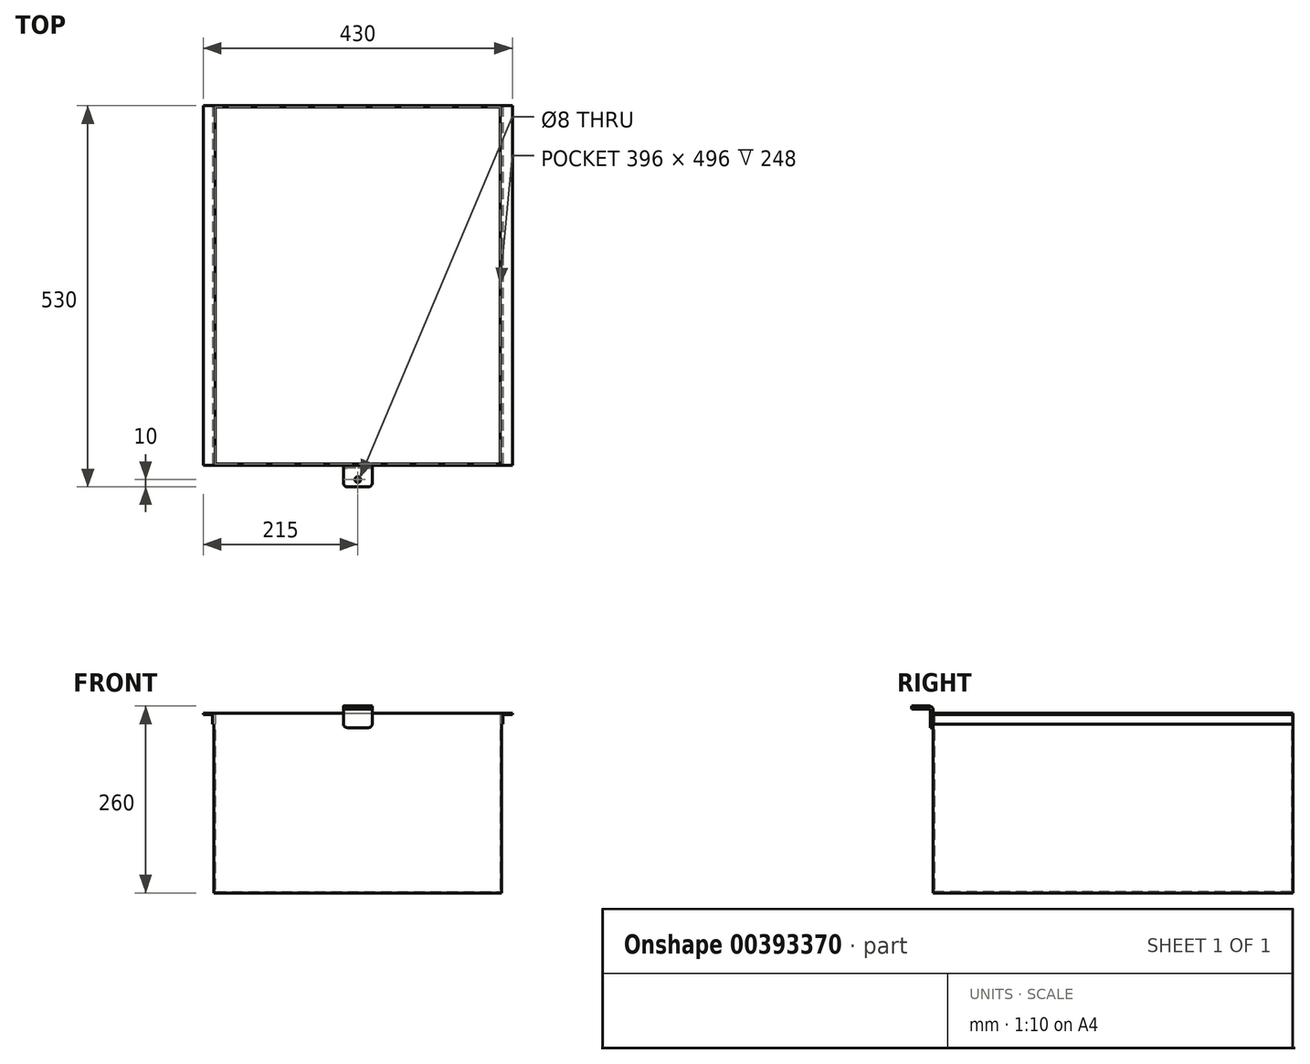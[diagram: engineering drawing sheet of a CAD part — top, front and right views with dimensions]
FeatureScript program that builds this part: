
annotation { "Feature Type Name" : "Feature", "Feature Type Description" : "" }
export const myFeature = defineFeature(function(context is Context, id is Id, definition is map)
    precondition{}
    {
        {
            var Q0;
            Q0=qCreatedBy(makeId("Top.planeOp"),FACE);
            var sketch = newSketch(context, id + "F0", { "sketchPlane" : qUnion([Q0])});
            skLineSegment(sketch, "E0.bottom", {"start": v(-200, 250) * mm, "end": v(200, 250) * mm});
            skLineSegment(sketch, "E0.top", {"start": v(-200, -250) * mm, "end": v(200, -250) * mm});
            skLineSegment(sketch, "E0.left", {"start": v(-200, 250) * mm, "end": v(-200, -250) * mm});
            skLineSegment(sketch, "E0.right", {"start": v(200, 250) * mm, "end": v(200, -250) * mm});
            skSolve(sketch);
        }
        {
            var Q0;
            Q0 = qSketchRegion(id + "F0", true);
            extrude(context, id + "F1", {"entities" : qUnion([Q0]), "depth" : 2 * mm, "offsetDistance" : 25 * mm});
        }
        {
            var Q0;
            Q0=makeQuery(id+"F1.opExtrude","CAP_FACE",FACE,{"disambiguationData":[OSD([sQuery(id+"F0.wireOp",EDGE,"E0.bottom"),sQuery(id+"F0.wireOp",EDGE,"E0.top"),sQuery(id+"F0.wireOp",EDGE,"E0.left"),sQuery(id+"F0.wireOp",EDGE,"E0.right")])],"isStart":false});
            var sketch = newSketch(context, id + "F2", { "sketchPlane" : qUnion([Q0])});
            skLineSegment(sketch, "E1.bottom", {"start": v(-200, 250) * mm, "end": v(200, 250) * mm});
            skLineSegment(sketch, "E1.top", {"start": v(-200, -250) * mm, "end": v(200, -250) * mm});
            skLineSegment(sketch, "E1.left", {"start": v(-200, 250) * mm, "end": v(-200, -250) * mm});
            skLineSegment(sketch, "E1.right", {"start": v(200, 250) * mm, "end": v(200, -250) * mm});
            skLineSegment(sketch, "E2.bottom", {"start": v(-198, 248) * mm, "end": v(198, 248) * mm});
            skLineSegment(sketch, "E2.top", {"start": v(-198, -248) * mm, "end": v(198, -248) * mm});
            skLineSegment(sketch, "E2.left", {"start": v(-198, 248) * mm, "end": v(-198, -248) * mm});
            skLineSegment(sketch, "E2.right", {"start": v(198, 248) * mm, "end": v(198, -248) * mm});
            skSolve(sketch);
        }
        {
            var Q0;
            Q0 = qSketchRegion(id + "F2", true);
            extrude(context, id + "F3", {"entities" : qUnion([Q0]), "operationType" : NewBodyOperationType.ADD, "depth" : 248 * mm, "offsetDistance" : 25 * mm});
        }
        {
            var Q0;
            Q0=makeQuery(id+"F3.boolean.opBoolean","MERGE",FACE,{"derivedFrom":[makeQuery(id+"F1.opExtrude","SWEPT_FACE",FACE,{"disambiguationData":[OSD([sQuery(id+"F0.wireOp",EDGE,"E0.top")])]}),makeQuery(id+"F3.opExtrude","SWEPT_FACE",FACE,{"disambiguationData":[OSD([sQuery(id+"F2.wireOp",EDGE,"E1.top")])]})]});
            var sketch = newSketch(context, id + "F4", { "sketchPlane" : qUnion([Q0])});
            skLineSegment(sketch, "E3", {"start": v(200, 250) * mm, "end": v(215, 250) * mm});
            skLineSegment(sketch, "E4", {"start": v(215, 250) * mm, "end": v(215, 248) * mm});
            skLineSegment(sketch, "E5", {"start": v(215, 248) * mm, "end": v(202, 248) * mm});
            skLineSegment(sketch, "E6", {"start": v(202, 248) * mm, "end": v(202, 235) * mm});
            skLineSegment(sketch, "E7", {"start": v(202, 235) * mm, "end": v(200, 235) * mm});
            skLineSegment(sketch, "E8", {"start": v(200, 235) * mm, "end": v(200, 250) * mm});
            skLineSegment(sketch, "E9.MirrorCS", {"start": v(-200, 250) * mm, "end": v(-215, 250) * mm});
            skLineSegment(sketch, "E10.MirrorCS", {"start": v(-215, 250) * mm, "end": v(-215, 248) * mm});
            skLineSegment(sketch, "E11.MirrorCS", {"start": v(-215, 248) * mm, "end": v(-202, 248) * mm});
            skLineSegment(sketch, "E12.MirrorCS", {"start": v(-202, 248) * mm, "end": v(-202, 235) * mm});
            skLineSegment(sketch, "E13.MirrorCS", {"start": v(-202, 235) * mm, "end": v(-200, 235) * mm});
            skLineSegment(sketch, "E14.MirrorCS", {"start": v(-200, 235) * mm, "end": v(-200, 250) * mm});
            skSolve(sketch);
        }
        {
            var Q0;
            Q0 = qSketchRegion(id + "F4", true);
            extrude(context, id + "F5", {"entities" : qUnion([Q0]), "operationType" : NewBodyOperationType.ADD, "oppositeDirection" : true, "depth" : 500 * mm, "offsetDistance" : 25 * mm});
        }
        {
            var Q0;
            Q0=qCreatedBy(makeId("Right.planeOp"),FACE);
            var sketch = newSketch(context, id + "F6", { "sketchPlane" : qUnion([Q0])});
            skLineSegment(sketch, "E15", {"start": v(-280, 260) * mm, "end": v(-256, 260) * mm});
            skLineSegment(sketch, "E16", {"start": v(-250, 254) * mm, "end": v(-250, 230) * mm});
            skLineSegment(sketch, "E17", {"start": v(-250, 230) * mm, "end": v(-254, 230) * mm});
            skLineSegment(sketch, "E18", {"start": v(-254, 230) * mm, "end": v(-254, 254) * mm});
            skLineSegment(sketch, "E19", {"start": v(-256, 256) * mm, "end": v(-280, 256) * mm});
            skLineSegment(sketch, "E20", {"start": v(-280, 256) * mm, "end": v(-280, 260) * mm});
            skPoint(sketch, "E21.visualSharp", {"position": v(-250, 250) * mm});
            skArc(sketch, "E21.filletArc", {"start": v(-250, 254) * mm, "mid": v(-251.76, 258.24) * mm, "end": v(-256, 260) * mm});
            skPoint(sketch, "E22.visualSharp", {"position": v(-254, 256) * mm});
            skArc(sketch, "E22.filletArc", {"start": v(-254, 254) * mm, "mid": v(-254.59, 255.41) * mm, "end": v(-256, 256) * mm});
            skSolve(sketch);
        }
        {
            var Q0;
            Q0 = qSketchRegion(id + "F6", true);
            extrude(context, id + "F7", {"entities" : qUnion([Q0]), "operationType" : NewBodyOperationType.ADD, "endBound" : BoundingType.SYMMETRIC, "depth" : 40 * mm, "offsetDistance" : 25 * mm});
        }
        {
            var Q0;
            Q0=makeQuery(id+"F7.opExtrude","CAP_EDGE",EDGE,{"disambiguationData":[OSD([sQuery(id+"F6.wireOp",EDGE,"E20")])],"isStart":false});
            var Q1;
            Q1=makeQuery(id+"F7.opExtrude","CAP_EDGE",EDGE,{"disambiguationData":[OSD([sQuery(id+"F6.wireOp",EDGE,"E20")])],"isStart":true});
            fillet(context, id + "F8", {"entities" : qUnion([Q0, Q1]), "radius" : 5 * mm, "tangentPropagation" : true, "allowEdgeOverflow" : false});
        }
        {
            var Q0;
            Q0=makeQuery(id+"F7.opExtrude","SWEPT_FACE",FACE,{"disambiguationData":[OSD([sQuery(id+"F6.wireOp",EDGE,"E15")])]});
            var sketch = newSketch(context, id + "F9", { "sketchPlane" : qUnion([Q0])});
            skSolve(sketch);
        }
        {
            var Q0;
            {var subQ0=sQuery(id+"F6.wireOp",EDGE,"E15");Q0=makeQuery(id+"F9.imprint","IMPRINT",FACE,{"disambiguationData":[TD([[makeQuery(id+"F9.imprint","IMPRINT",EDGE,{"derivedFrom":makeQuery(id+"F7.opExtrude","CAP_EDGE",EDGE,{"disambiguationData":[OSD([subQ0])],"isStart":true})}),-1.0]])]});}
            var sketch = newSketch(context, id + "F10", { "sketchPlane" : qUnion([Q0])});
            skCircle(sketch, "E23", {"center": v(0, -270) * mm, "radius": 4 * mm});
            skSolve(sketch);
        }
        {
            var Q0;
            Q0=makeQuery(id+"F10.imprint","IMPRINT",FACE,{"disambiguationData":[TD([[makeQuery(id+"F10.imprint","IMPRINT",EDGE,{"derivedFrom":sQuery(id+"F10.wireOp",EDGE,"E23")}),1.0]])]});
            extrude(context, id + "F11", {"entities" : qUnion([Q0]), "operationType" : NewBodyOperationType.REMOVE, "oppositeDirection" : true, "depth" : 25 * mm, "offsetDistance" : 25 * mm});
        }
        {
            var Q0;
            Q0=makeQuery(id+"F7.opExtrude","CAP_EDGE",EDGE,{"disambiguationData":[OSD([sQuery(id+"F6.wireOp",EDGE,"E17")])],"isStart":false});
            var Q1;
            Q1=makeQuery(id+"F7.opExtrude","CAP_EDGE",EDGE,{"disambiguationData":[OSD([sQuery(id+"F6.wireOp",EDGE,"E17")])],"isStart":true});
            fillet(context, id + "F12", {"entities" : qUnion([Q0, Q1]), "radius" : 5 * mm, "tangentPropagation" : true, "allowEdgeOverflow" : false});
        }
    });
